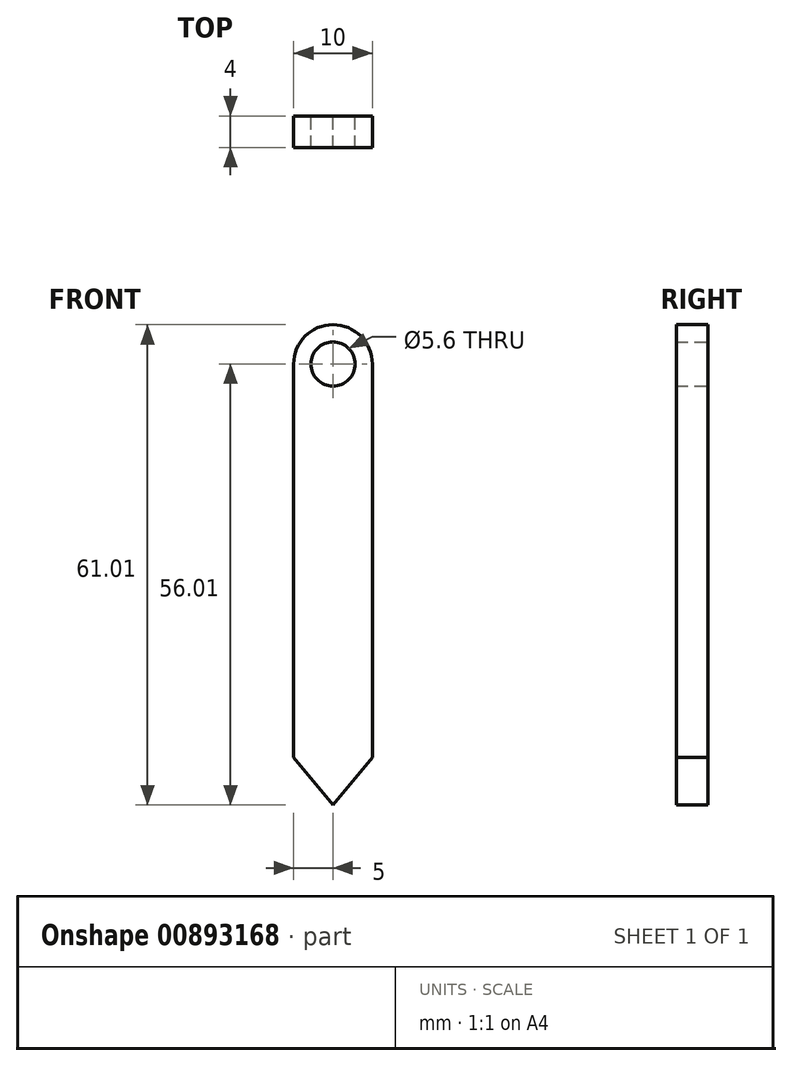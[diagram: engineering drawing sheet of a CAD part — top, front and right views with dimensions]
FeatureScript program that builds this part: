
annotation { "Feature Type Name" : "Feature", "Feature Type Description" : "" }
export const myFeature = defineFeature(function(context is Context, id is Id, definition is map)
    precondition{}
    {
        {
            var Q0;
            Q0=qCreatedBy(makeId("Front.planeOp"),FACE);
            var sketch = newSketch(context, id + "F0", { "sketchPlane" : qUnion([Q0])});
            skCircle(sketch, "E0", {"center": v(0, 0) * mm, "radius": 2.8 * mm});
            skCircle(sketch, "E1", {"center": v(0, 0) * mm, "radius": 5 * mm});
            skLineSegment(sketch, "E2", {"start": v(-5, 0) * mm, "end": v(-5, -50) * mm});
            skLineSegment(sketch, "E3", {"start": v(5, 0) * mm, "end": v(5, -50) * mm});
            skLineSegment(sketch, "E4", {"start": v(-5, -50) * mm, "end": v(0, -56.01) * mm});
            skLineSegment(sketch, "E5", {"start": v(0, -56.01) * mm, "end": v(5, -50) * mm});
            skSolve(sketch);
        }
        {
            var Q0;
            Q0=makeQuery(id+"F0.imprint","IMPRINT",FACE,{"disambiguationData":[TD([[makeQuery(id+"F0.imprint","IMPRINT",EDGE,{"derivedFrom":sQuery(id+"F0.wireOp",EDGE,"E0")}),-1.0]])]});
            var Q1;
            {var subQ1=sQuery(id+"F0.wireOp",EDGE,"E2");Q1=makeQuery(id+"F0.imprint","IMPRINT",FACE,{"disambiguationData":[TD([[makeQuery(id+"F0.imprint","IMPRINT",EDGE,{"derivedFrom":subQ1}),1.0]])]});}
            extrude(context, id + "F1", {"entities" : qUnion([Q0, Q1]), "depth" : 4 * mm, "offsetDistance" : 25 * mm});
        }
    });
